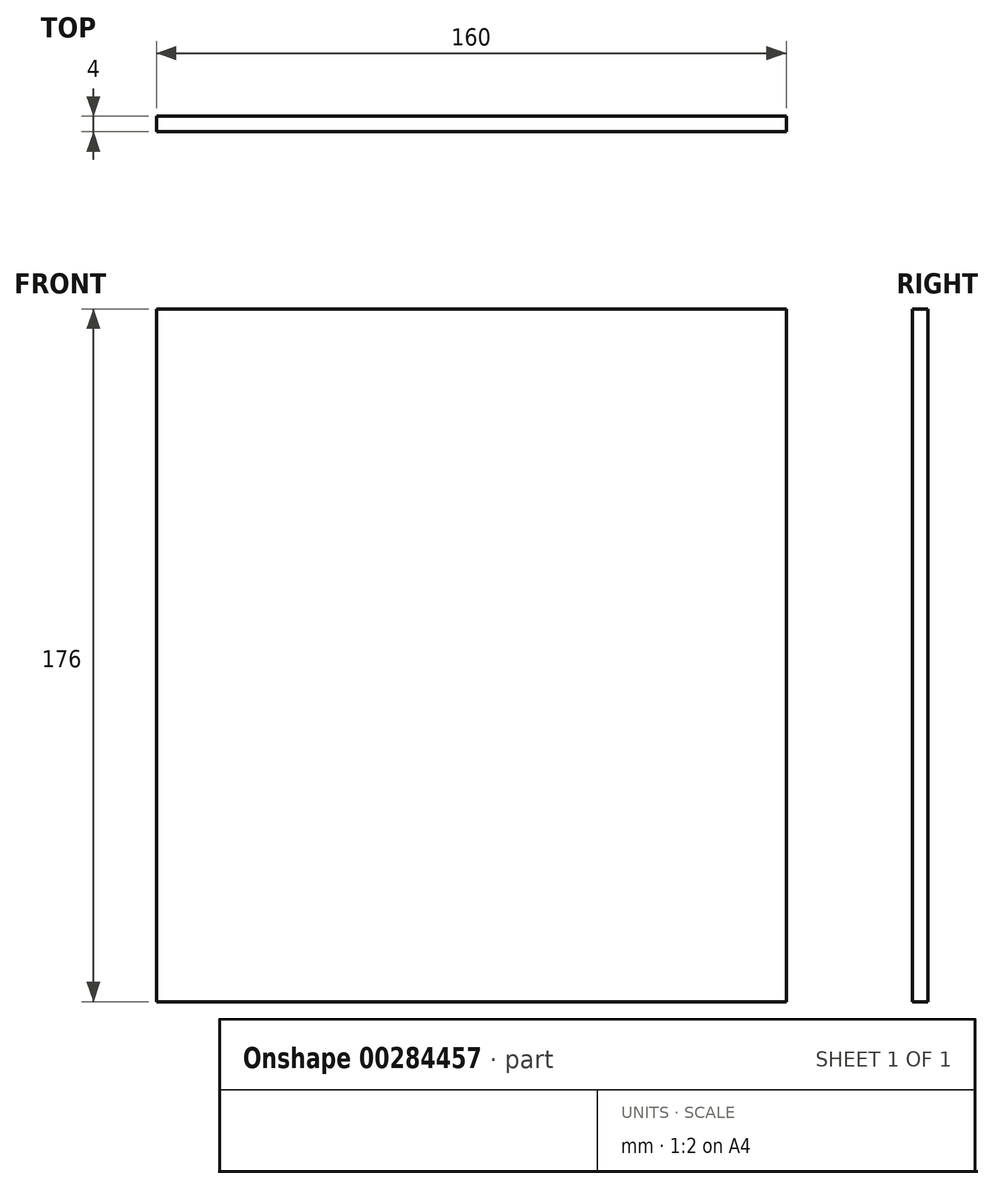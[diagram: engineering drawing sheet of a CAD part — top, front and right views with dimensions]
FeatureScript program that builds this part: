
annotation { "Feature Type Name" : "Feature", "Feature Type Description" : "" }
export const myFeature = defineFeature(function(context is Context, id is Id, definition is map)
    precondition{}
    {
        {
            var Q0;
            Q0=qCreatedBy(makeId("Front.planeOp"),FACE);
            var sketch = newSketch(context, id + "F0", { "sketchPlane" : qUnion([Q0])});
            skLineSegment(sketch, "E0.bottom", {"start": v(80, -88) * mm, "end": v(-80, -88) * mm});
            skLineSegment(sketch, "E0.top", {"start": v(80, 88) * mm, "end": v(-80, 88) * mm});
            skLineSegment(sketch, "E0.left", {"start": v(80, -88) * mm, "end": v(80, 88) * mm});
            skLineSegment(sketch, "E0.right", {"start": v(-80, -88) * mm, "end": v(-80, 88) * mm});
            skPoint(sketch, "E0.middle", {"position": v(0, 0) * mm});
            skSolve(sketch);
        }
        {
            var Q0;
            Q0=makeQuery(id+"F0.imprint","IMPRINT",FACE,{"disambiguationData":[TD([[makeQuery(id+"F0.imprint","IMPRINT",EDGE,{"derivedFrom":sQuery(id+"F0.wireOp",EDGE,"E0.bottom")}),-1.0]])]});
            extrude(context, id + "F1", {"entities" : qUnion([Q0]), "depth" : 4 * mm});
        }
    });
